# Revit family: 734250001_Ducha Electrica 110V Megaducha
name_source: partatom
category: Plumbing Fixtures
units: mm (PartAtom-declared; Revit-internal decimal feet)

## family parameters
Always vertical = Yes
Cut with Voids When Loaded = No
Host = Wall
OmniClass Number = 23.31.17.00
OmniClass Title = Showers
Part Type = Normal
Room Calculation Point = No
Round Connector Dimension = Use Diameter
Shared = No

## types (1)
- Type 1
    Cableado mínimo = 10 mm2 - 8 AWG
    Corriente Nominal = 36.8 A
    Creado por = BIMBAU
    Default Elevation = 0 mm  [stored 0 ft]
    Description = Ducha eléctrica con certificación RETIE fabricado en aleaciones de cobre, acero, plata, níquel, cromo, aluminio, elastómeros y termoplásticos. 3 temperaturas (FRIO, TÍBIO Y CALIENTE) es posible alcanzar la temperatura ideal y tener el consumo de energía eléctrica de acuerdo a la necesidad. En días y/o regiones más frías, se puede disfrutar de agua caliente en la posición CALIENTE y en días calientes, la economía puede alcanzar 65%, utilizando la ducha en la posición TÍBIA.
    Dimensión de la regadera = 150 x 121 x 121 mm
    Diámetro = 100 mm  [stored 0.328084 ft]
    Fecha de creación = 21/06/2021
    Garantía = 2 años
    Grado de protección = IP24
    Interruptor Requerido = 40 A
    Largo = 140 mm  [stored 0.459318 ft]
    Manufacturer = Grival
    Material = Corona_Plastico_Blanco
    Normatividad = NBR 12483, NBR 12087, NBR 12089, NBR 12090
    Peso neto = 390 g. - 0.86 lb
    Potencia Nominal = 4050 W
    Presión máxima recomendada = 58 psi
    Presión mínima recomendada = 14.5 psi
    Productos compatibles = Brazo DH Electrica con malla, Brazo DH Electrica Telescopio
    Referencia = 734250001
    Resistencia = Resistente a la corrosión, pelado y decoloración por agua
    Resistividad mínima del agua = 1300 Ω cm
    Temperatura de uso = Entre 5˚C / 41 ° F a 71˚C / 159,8 °F
    Tensión nominal = 110 V
    URL = https://www.grival.com
    Uso = Residencial

note: [stored X ft] marks values corroborated as IEEE doubles in the binary element streams (Revit-internal decimal feet)

## geometry (parser evidence)
native form markers: Sweep x3
no freeform markers — native parametric forms only
